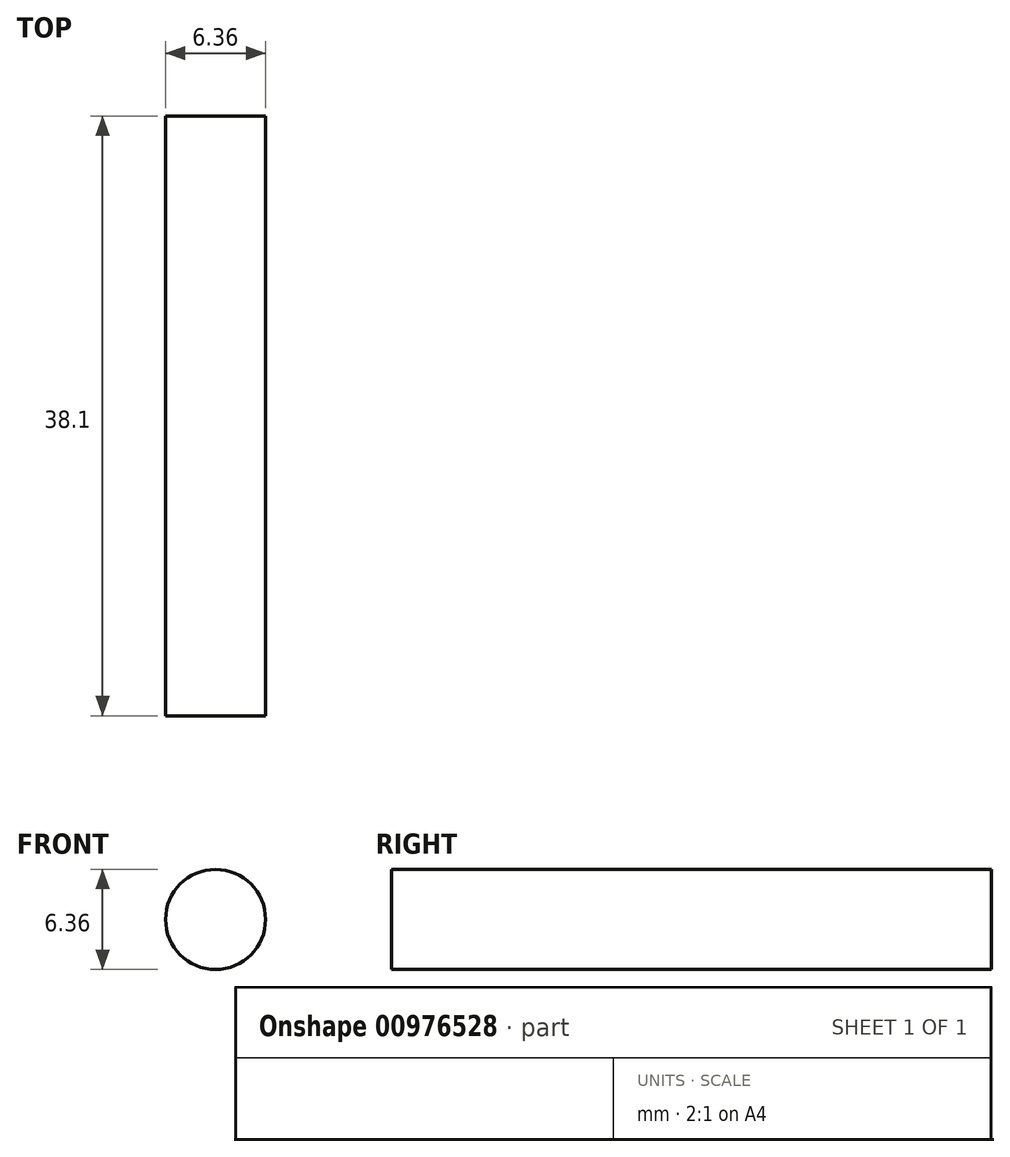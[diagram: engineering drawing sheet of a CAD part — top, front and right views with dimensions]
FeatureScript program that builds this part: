
annotation { "Feature Type Name" : "Feature", "Feature Type Description" : "" }
export const myFeature = defineFeature(function(context is Context, id is Id, definition is map)
    precondition{}
    {
        {
            var Q0;
            Q0=qCreatedBy(makeId("Front.planeOp"),FACE);
            var sketch = newSketch(context, id + "F0", { "sketchPlane" : qUnion([Q0])});
            skCircle(sketch, "E0", {"center": v(0, 0) * mm, "radius": 3.18 * mm});
            skSolve(sketch);
        }
        {
            var Q0;
            Q0=makeQuery(id+"F0.imprint","IMPRINT",FACE,{"disambiguationData":[TD([[makeQuery(id+"F0.imprint","IMPRINT",EDGE,{"derivedFrom":sQuery(id+"F0.wireOp",EDGE,"E0")}),1.0]])]});
            extrude(context, id + "F1", {"entities" : qUnion([Q0]), "depth" : 38.1 * mm, "offsetDistance" : 25.4 * mm});
        }
    });
